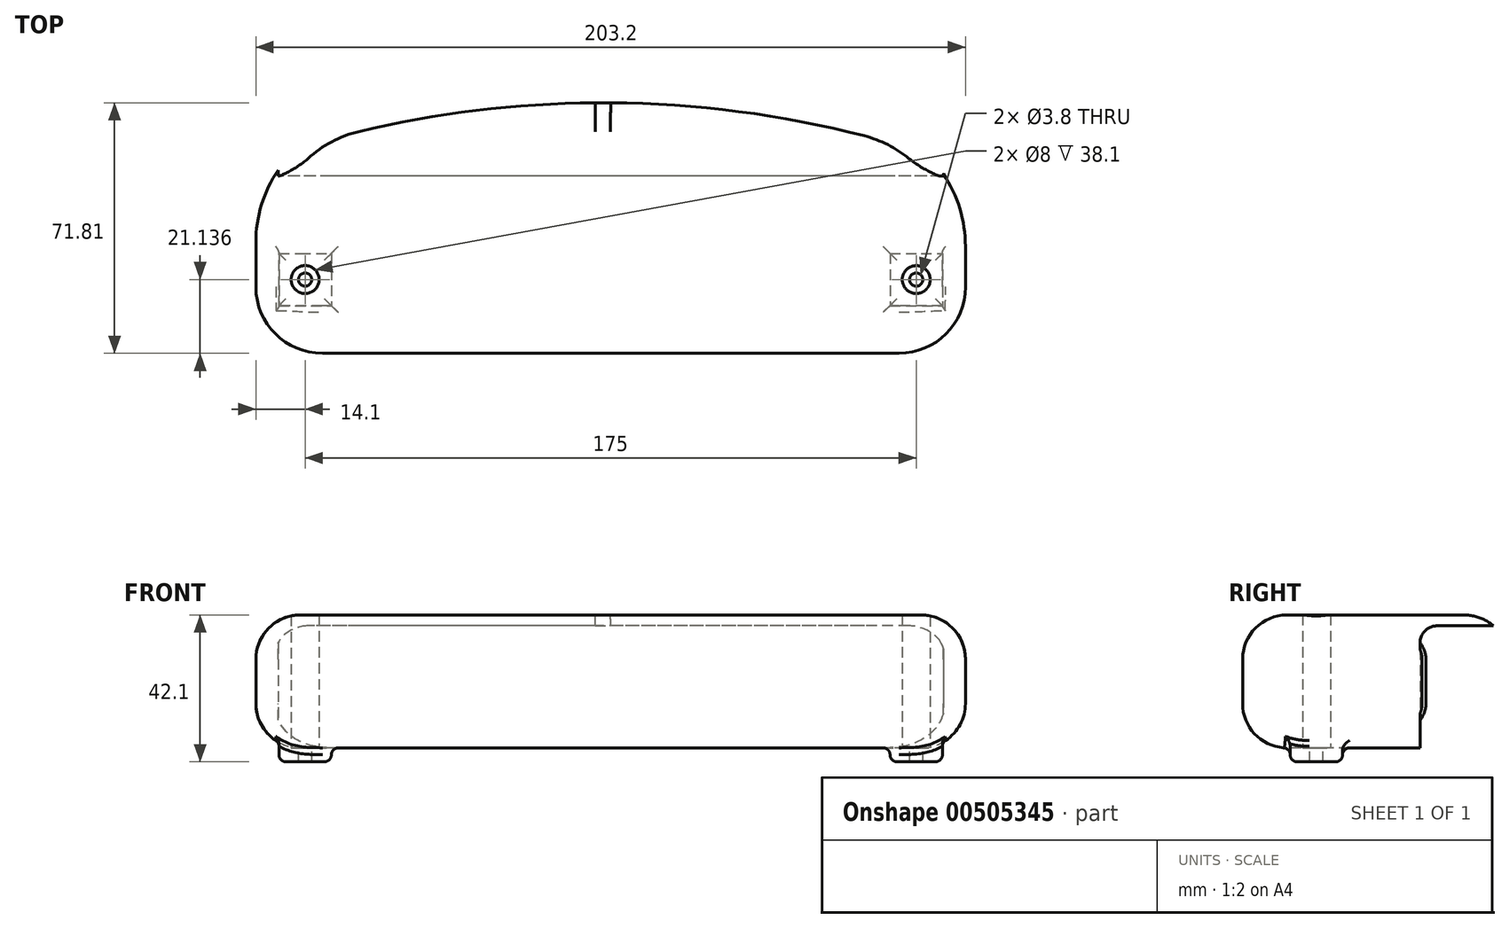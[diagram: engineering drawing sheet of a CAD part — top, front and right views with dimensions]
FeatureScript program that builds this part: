
annotation { "Feature Type Name" : "Feature", "Feature Type Description" : "" }
export const myFeature = defineFeature(function(context is Context, id is Id, definition is map)
    precondition{}
    {
        {
            var Q0;
            Q0=qCreatedBy(makeId("Top.planeOp"),FACE);
            var sketch = newSketch(context, id + "F0", { "sketchPlane" : qUnion([Q0])});
            skLineSegment(sketch, "E0.bottom", {"start": v(82.55, -38.1) * mm, "end": v(-82.55, -38.1) * mm});
            skLineSegment(sketch, "E0.top", {"start": v(0, 38.1) * mm, "end": v(-4.47, 38.1) * mm});
            skLineSegment(sketch, "E0.left", {"start": v(101.6, -19.05) * mm, "end": v(101.6, -7.46) * mm});
            skLineSegment(sketch, "E0.right", {"start": v(-101.6, -19.05) * mm, "end": v(-101.6, -6.35) * mm});
            skPoint(sketch, "E0.middle", {"position": v(0, 0) * mm});
            skPoint(sketch, "E1.visualSharp", {"position": v(-101.6, -38.1) * mm});
            skArc(sketch, "E1.filletArc", {"start": v(-101.6, -19.05) * mm, "mid": v(-96.02, -32.52) * mm, "end": v(-82.55, -38.1) * mm});
            skPoint(sketch, "E2.visualSharp", {"position": v(101.6, -38.1) * mm});
            skArc(sketch, "E2.filletArc", {"start": v(82.55, -38.1) * mm, "mid": v(96.02, -32.52) * mm, "end": v(101.6, -19.05) * mm});
            skArc(sketch, "E3", {"start": v(73.73, 28.49) * mm, "mid": v(0.39, 38.1) * mm, "end": v(-73.11, 29.75) * mm});
            skPoint(sketch, "E4", {"position": v(0, 38.1) * mm});
            skArc(sketch, "E5", {"start": v(-73.11, 29.75) * mm, "mid": v(-93.62, 16.65) * mm, "end": v(-101.6, -6.35) * mm});
            skArc(sketch, "E6", {"start": v(101.6, -7.46) * mm, "mid": v(93.82, 15.28) * mm, "end": v(73.73, 28.49) * mm});
            skPoint(sketch, "E7.orphan", {"position": v(101.6, 38.1) * mm});
            skPoint(sketch, "E8.trimOffspring.end.orphan", {"position": v(-101.6, 38.1) * mm});
            skPoint(sketch, "E9", {"position": v(-87.5, -16.96) * mm});
            skPoint(sketch, "E10", {"position": v(87.5, -16.96) * mm});
            skLineSegment(sketch, "E11", {"start": v(0, 0) * mm, "end": v(0, -38.1) * mm});
            skSolve(sketch);
        }
        {
            var Q0;
            Q0=makeQuery(id+"F0.imprint","IMPRINT",FACE,{"disambiguationData":[TD([[makeQuery(id+"F0.imprint","IMPRINT",EDGE,{"derivedFrom":sQuery(id+"F0.wireOp",EDGE,"E0.bottom")}),-1.0]])]});
            extrude(context, id + "F1", {"entities" : qUnion([Q0]), "depth" : 38.1 * mm});
        }
        {
            var Q0;
            Q0=makeQuery(id+"F1.opExtrude","CAP_EDGE",EDGE,{"disambiguationData":[OSD([sQuery(id+"F0.wireOp",EDGE,"E0.bottom")])],"isStart":false});
            var Q1;
            {var subQ0=sQuery(id+"F0.wireOp",EDGE,"E3");Q1=makeQuery(id+"F1.opExtrude","CAP_EDGE",EDGE,{"disambiguationData":[OSD([subQ0]),TDD([makeQuery(id+"F0.imprint","IMPRINT",EDGE,{"disambiguationData":[TD([[makeQuery(id+"F0.imprint","INTERSECT",VERTEX,{"disambiguationData":[OD(0.0)],"derivedFrom":[sQuery(id+"F0.wireOp",EDGE,"E0.top"),subQ0]}),1.0]])],"derivedFrom":subQ0})])],"isStart":true});}
            fillet(context, id + "F2", {"entities" : qUnion([Q0, Q1]), "radius" : 12.7 * mm, "tangentPropagation" : true, "allowEdgeOverflow" : false});
        }
        {
            var Q0;
            Q0=makeQuery(id+"F1.opExtrude","CAP_FACE",FACE,{"disambiguationData":[OSD([sQuery(id+"F0.wireOp",EDGE,"E0.bottom"),sQuery(id+"F0.wireOp",EDGE,"E0.top"),sQuery(id+"F0.wireOp",EDGE,"E0.left"),sQuery(id+"F0.wireOp",EDGE,"E0.right"),sQuery(id+"F0.wireOp",EDGE,"E1.filletArc"),sQuery(id+"F0.wireOp",EDGE,"E2.filletArc"),sQuery(id+"F0.wireOp",EDGE,"E3"),sQuery(id+"F0.wireOp",EDGE,"E5"),sQuery(id+"F0.wireOp",EDGE,"E6")])],"isStart":true});
            var sketch = newSketch(context, id + "F3", { "sketchPlane" : qUnion([Q0])});
            skLineSegment(sketch, "E12.bottom", {"start": v(80, 9.46) * mm, "end": v(95, 9.46) * mm});
            skLineSegment(sketch, "E12.top", {"start": v(80, 24.46) * mm, "end": v(95, 24.46) * mm});
            skLineSegment(sketch, "E12.left", {"start": v(80, 9.46) * mm, "end": v(80, 24.46) * mm});
            skLineSegment(sketch, "E12.right", {"start": v(95, 9.46) * mm, "end": v(95, 24.46) * mm});
            skPoint(sketch, "E12.middle", {"position": v(87.5, 16.96) * mm});
            skPoint(sketch, "E12.middle.positionSnap0", {"position": v(87.04, 23.54) * mm});
            skPoint(sketch, "E12.centerSnap0", {"position": v(87.04, 23.54) * mm});
            skLineSegment(sketch, "E13.bottom", {"start": v(-95, 9.46) * mm, "end": v(-80, 9.46) * mm});
            skLineSegment(sketch, "E13.top", {"start": v(-95, 24.46) * mm, "end": v(-80, 24.46) * mm});
            skLineSegment(sketch, "E13.left", {"start": v(-95, 9.46) * mm, "end": v(-95, 24.46) * mm});
            skLineSegment(sketch, "E13.right", {"start": v(-80, 9.46) * mm, "end": v(-80, 24.46) * mm});
            skPoint(sketch, "E13.middle", {"position": v(-87.5, 16.96) * mm});
            skSolve(sketch);
        }
        {
            var Q0;
            Q0 = qSketchRegion(id + "F3", true);
            extrude(context, id + "F4", {"entities" : qUnion([Q0]), "operationType" : NewBodyOperationType.ADD, "depth" : 4 * mm, "hasSecondDirection" : true, "secondDirectionOppositeDirection" : true, "secondDirectionDepth" : 8 * mm});
        }
        {
            var Q0;
            Q0=makeQuery(id+"F4.opExtrude","CAP_EDGE",EDGE,{"disambiguationData":[OSD([sQuery(id+"F3.wireOp",EDGE,"E12.right")])],"isStart":false});
            var Q1;
            {var subQ0=sQuery(id+"F0.wireOp",EDGE,"E0.left");Q1=makeQuery(id+"F4.boolean.opBoolean","INTERSECT",EDGE,{"derivedFrom":[makeQuery(id+"F2.opFillet","BLEND_FACE",FACE,{"disambiguationData":[OSD([subQ0]),TDD([makeQuery(id+"F1.opExtrude","CAP_EDGE",EDGE,{"disambiguationData":[OSD([subQ0])],"isStart":true})])]}),makeQuery(id+"F4.opExtrude","SWEPT_FACE",FACE,{"disambiguationData":[OSD([sQuery(id+"F3.wireOp",EDGE,"E12.right")])]})]});}
            var Q2;
            Q2=makeQuery(id+"F4.boolean.opBoolean","INTERSECT",EDGE,{"derivedFrom":[makeQuery(id+"F1.opExtrude","CAP_FACE",FACE,{"disambiguationData":[OSD([sQuery(id+"F0.wireOp",EDGE,"E0.bottom"),sQuery(id+"F0.wireOp",EDGE,"E0.top"),sQuery(id+"F0.wireOp",EDGE,"E0.left"),sQuery(id+"F0.wireOp",EDGE,"E0.right"),sQuery(id+"F0.wireOp",EDGE,"E1.filletArc"),sQuery(id+"F0.wireOp",EDGE,"E2.filletArc"),sQuery(id+"F0.wireOp",EDGE,"E3"),sQuery(id+"F0.wireOp",EDGE,"E5"),sQuery(id+"F0.wireOp",EDGE,"E6")])],"isStart":true}),makeQuery(id+"F4.opExtrude","SWEPT_FACE",FACE,{"disambiguationData":[OSD([sQuery(id+"F3.wireOp",EDGE,"E12.left")])]})]});
            var Q3;
            Q3=makeQuery(id+"F4.boolean.opBoolean","INTERSECT",EDGE,{"derivedFrom":[makeQuery(id+"F1.opExtrude","CAP_FACE",FACE,{"disambiguationData":[OSD([sQuery(id+"F0.wireOp",EDGE,"E0.bottom"),sQuery(id+"F0.wireOp",EDGE,"E0.top"),sQuery(id+"F0.wireOp",EDGE,"E0.left"),sQuery(id+"F0.wireOp",EDGE,"E0.right"),sQuery(id+"F0.wireOp",EDGE,"E1.filletArc"),sQuery(id+"F0.wireOp",EDGE,"E2.filletArc"),sQuery(id+"F0.wireOp",EDGE,"E3"),sQuery(id+"F0.wireOp",EDGE,"E5"),sQuery(id+"F0.wireOp",EDGE,"E6")])],"isStart":true}),makeQuery(id+"F4.opExtrude","SWEPT_FACE",FACE,{"disambiguationData":[OSD([sQuery(id+"F3.wireOp",EDGE,"E12.bottom")])]})]});
            var Q4;
            Q4=makeQuery(id+"F4.opExtrude","CAP_EDGE",EDGE,{"disambiguationData":[OSD([sQuery(id+"F3.wireOp",EDGE,"E12.bottom")])],"isStart":false});
            var Q5;
            Q5=makeQuery(id+"F4.opExtrude","CAP_EDGE",EDGE,{"disambiguationData":[OSD([sQuery(id+"F3.wireOp",EDGE,"E12.left")])],"isStart":false});
            var Q6;
            {var subQ0=sQuery(id+"F0.wireOp",EDGE,"E2.filletArc");Q6=makeQuery(id+"F4.boolean.opBoolean","INTERSECT",EDGE,{"derivedFrom":[makeQuery(id+"F2.opFillet","BLEND_FACE",FACE,{"disambiguationData":[OSD([subQ0]),TDD([makeQuery(id+"F1.opExtrude","CAP_EDGE",EDGE,{"disambiguationData":[OSD([subQ0])],"isStart":true})])]}),makeQuery(id+"F4.opExtrude","SWEPT_FACE",FACE,{"disambiguationData":[OSD([sQuery(id+"F3.wireOp",EDGE,"E12.top")])]})]});}
            var Q7;
            Q7=makeQuery(id+"F4.opExtrude","CAP_EDGE",EDGE,{"disambiguationData":[OSD([sQuery(id+"F3.wireOp",EDGE,"E12.top")])],"isStart":false});
            var Q8;
            Q8=makeQuery(id+"F4.opExtrude","CAP_EDGE",EDGE,{"disambiguationData":[OSD([sQuery(id+"F3.wireOp",EDGE,"E13.top")])],"isStart":false});
            var Q9;
            Q9=makeQuery(id+"F4.opExtrude","CAP_EDGE",EDGE,{"disambiguationData":[OSD([sQuery(id+"F3.wireOp",EDGE,"E13.right")])],"isStart":false});
            var Q10;
            Q10=makeQuery(id+"F4.opExtrude","CAP_EDGE",EDGE,{"disambiguationData":[OSD([sQuery(id+"F3.wireOp",EDGE,"E13.bottom")])],"isStart":false});
            var Q11;
            Q11=makeQuery(id+"F4.opExtrude","CAP_EDGE",EDGE,{"disambiguationData":[OSD([sQuery(id+"F3.wireOp",EDGE,"E13.left")])],"isStart":false});
            var Q12;
            Q12=makeQuery(id+"F4.boolean.opBoolean","INTERSECT",EDGE,{"derivedFrom":[makeQuery(id+"F1.opExtrude","CAP_FACE",FACE,{"disambiguationData":[OSD([sQuery(id+"F0.wireOp",EDGE,"E0.bottom"),sQuery(id+"F0.wireOp",EDGE,"E0.top"),sQuery(id+"F0.wireOp",EDGE,"E0.left"),sQuery(id+"F0.wireOp",EDGE,"E0.right"),sQuery(id+"F0.wireOp",EDGE,"E1.filletArc"),sQuery(id+"F0.wireOp",EDGE,"E2.filletArc"),sQuery(id+"F0.wireOp",EDGE,"E3"),sQuery(id+"F0.wireOp",EDGE,"E5"),sQuery(id+"F0.wireOp",EDGE,"E6")])],"isStart":true}),makeQuery(id+"F4.opExtrude","SWEPT_FACE",FACE,{"disambiguationData":[OSD([sQuery(id+"F3.wireOp",EDGE,"E13.top")])]})]});
            var Q13;
            Q13=makeQuery(id+"F4.boolean.opBoolean","INTERSECT",EDGE,{"derivedFrom":[makeQuery(id+"F1.opExtrude","CAP_FACE",FACE,{"disambiguationData":[OSD([sQuery(id+"F0.wireOp",EDGE,"E0.bottom"),sQuery(id+"F0.wireOp",EDGE,"E0.top"),sQuery(id+"F0.wireOp",EDGE,"E0.left"),sQuery(id+"F0.wireOp",EDGE,"E0.right"),sQuery(id+"F0.wireOp",EDGE,"E1.filletArc"),sQuery(id+"F0.wireOp",EDGE,"E2.filletArc"),sQuery(id+"F0.wireOp",EDGE,"E3"),sQuery(id+"F0.wireOp",EDGE,"E5"),sQuery(id+"F0.wireOp",EDGE,"E6")])],"isStart":true}),makeQuery(id+"F4.opExtrude","SWEPT_FACE",FACE,{"disambiguationData":[OSD([sQuery(id+"F3.wireOp",EDGE,"E13.right")])]})]});
            var Q14;
            {var subQ0=sQuery(id+"F0.wireOp",EDGE,"E0.right");Q14=makeQuery(id+"F4.boolean.opBoolean","INTERSECT",EDGE,{"derivedFrom":[makeQuery(id+"F2.opFillet","BLEND_FACE",FACE,{"disambiguationData":[OSD([subQ0]),TDD([makeQuery(id+"F1.opExtrude","CAP_EDGE",EDGE,{"disambiguationData":[OSD([subQ0])],"isStart":true})])]}),makeQuery(id+"F4.opExtrude","SWEPT_FACE",FACE,{"disambiguationData":[OSD([sQuery(id+"F3.wireOp",EDGE,"E13.left")])]})]});}
            var Q15;
            Q15=makeQuery(id+"F4.boolean.opBoolean","INTERSECT",EDGE,{"derivedFrom":[makeQuery(id+"F1.opExtrude","CAP_FACE",FACE,{"disambiguationData":[OSD([sQuery(id+"F0.wireOp",EDGE,"E0.bottom"),sQuery(id+"F0.wireOp",EDGE,"E0.top"),sQuery(id+"F0.wireOp",EDGE,"E0.left"),sQuery(id+"F0.wireOp",EDGE,"E0.right"),sQuery(id+"F0.wireOp",EDGE,"E1.filletArc"),sQuery(id+"F0.wireOp",EDGE,"E2.filletArc"),sQuery(id+"F0.wireOp",EDGE,"E3"),sQuery(id+"F0.wireOp",EDGE,"E5"),sQuery(id+"F0.wireOp",EDGE,"E6")])],"isStart":true}),makeQuery(id+"F4.opExtrude","SWEPT_FACE",FACE,{"disambiguationData":[OSD([sQuery(id+"F3.wireOp",EDGE,"E13.bottom")])]})]});
            fillet(context, id + "F5", {"entities" : qUnion([Q0, Q1, Q2, Q3, Q4, Q5, Q6, Q7, Q8, Q9, Q10, Q11, Q12, Q13, Q14, Q15]), "radius" : 2 * mm, "tangentPropagation" : true, "allowEdgeOverflow" : false});
        }
        {
            var Q0;
            Q0=qCreatedBy(makeId("Top.planeOp"),FACE);
            var sketch = newSketch(context, id + "F6", { "sketchPlane" : qUnion([Q0])});
            skLineSegment(sketch, "E14.bottom", {"start": v(95.25, 12.7) * mm, "end": v(-95.25, 12.7) * mm});
            skLineSegment(sketch, "E14.top", {"start": v(95.25, 63.5) * mm, "end": v(-95.25, 63.5) * mm});
            skLineSegment(sketch, "E14.left", {"start": v(95.25, 12.7) * mm, "end": v(95.25, 63.5) * mm});
            skLineSegment(sketch, "E14.right", {"start": v(-95.25, 12.7) * mm, "end": v(-95.25, 63.5) * mm});
            skPoint(sketch, "E14.middle", {"position": v(0, 38.1) * mm});
            skSolve(sketch);
        }
        {
            var Q0;
            Q0=makeQuery(id+"F6.imprint","IMPRINT",FACE,{"disambiguationData":[TD([[makeQuery(id+"F6.imprint","IMPRINT",EDGE,{"derivedFrom":sQuery(id+"F6.wireOp",EDGE,"E14.bottom")}),-1.0]])]});
            extrude(context, id + "F7", {"entities" : qUnion([Q0]), "operationType" : NewBodyOperationType.REMOVE, "depth" : 35 * mm});
        }
        {
            var Q0;
            {var subQ0=sQuery(id+"F0.wireOp",EDGE,"E6");var subQ1=makeQuery(id+"F2.opFillet","BLEND_FACE",FACE,{"disambiguationData":[OSD([subQ0]),TDD([makeQuery(id+"F1.opExtrude","CAP_EDGE",EDGE,{"disambiguationData":[OSD([subQ0])],"isStart":false})])]});var subQ2=sQuery(id+"F6.wireOp",EDGE,"E14.bottom");Q0=makeQuery(id+"F7.boolean.opBoolean","COPY",EDGE,{"disambiguationData":[TD([subQ1])],"derivedFrom":makeQuery(id+"F7.opExtrude","CAP_EDGE",EDGE,{"disambiguationData":[OSD([subQ2])],"isStart":false})});}
            var Q1;
            {var subQ0=sQuery(id+"F0.wireOp",EDGE,"E5");var subQ1=makeQuery(id+"F2.opFillet","BLEND_FACE",FACE,{"disambiguationData":[OSD([subQ0]),TDD([makeQuery(id+"F1.opExtrude","CAP_EDGE",EDGE,{"disambiguationData":[OSD([subQ0])],"isStart":false})])]});var subQ2=sQuery(id+"F6.wireOp",EDGE,"E14.bottom");Q1=makeQuery(id+"F7.boolean.opBoolean","COPY",EDGE,{"disambiguationData":[TD([subQ1])],"derivedFrom":makeQuery(id+"F7.opExtrude","CAP_EDGE",EDGE,{"disambiguationData":[OSD([subQ2])],"isStart":false})});}
            fillet(context, id + "F8", {"entities" : qUnion([Q0, Q1]), "radius" : 5 * mm, "tangentPropagation" : true, "allowEdgeOverflow" : false});
        }
        {
            var Q0;
            Q0=sQuery(id+"F0.wireOp",VERTEX,"E10");
            var Q1;
            Q1=sQuery(id+"F0.wireOp",VERTEX,"E9");
            var Q2;
            Q2=makeQuery(id+"F1.opExtrude","SWEPT_BODY",BODY,{"disambiguationData":[OSD([sQuery(id+"F0.wireOp",EDGE,"E0.bottom"),sQuery(id+"F0.wireOp",EDGE,"E0.top"),sQuery(id+"F0.wireOp",EDGE,"E0.left"),sQuery(id+"F0.wireOp",EDGE,"E0.right"),sQuery(id+"F0.wireOp",EDGE,"E1.filletArc"),sQuery(id+"F0.wireOp",EDGE,"E2.filletArc"),sQuery(id+"F0.wireOp",EDGE,"E3"),sQuery(id+"F0.wireOp",EDGE,"E5"),sQuery(id+"F0.wireOp",EDGE,"E6")])]});
            hole(context, id + "F9", {"style" : HoleStyle.SIMPLE, "endStyle" : HoleEndStyle.THROUGH, "standardTappedOrClearance" : lookupTablePath({ "standard" : "ANSI", "fit" : "Normal (ASME)", "size" : "#6", "type" : "Clearance" }), "standardBlindInLast" : lookupTablePath({ "fit" : "Free", "standard" : "ANSI", "size" : "#6", "type" : "Clearance" }), "holeDiameter" : 3.8 * mm, "isTappedThrough" : true, "tappedDepth" : 12.7 * mm, "tapClearance" : 3, "locations" : qUnion([Q0, Q1]), "scope" : qUnion([Q2])});
        }
        {
            var Q0;
            Q0=sQuery(id+"F0.wireOp",VERTEX,"E9");
            var Q1;
            Q1=sQuery(id+"F0.wireOp",VERTEX,"E10");
            var Q2;
            Q2=makeQuery(id+"F1.opExtrude","SWEPT_BODY",BODY,{"disambiguationData":[OSD([sQuery(id+"F0.wireOp",EDGE,"E0.bottom"),sQuery(id+"F0.wireOp",EDGE,"E0.top"),sQuery(id+"F0.wireOp",EDGE,"E0.left"),sQuery(id+"F0.wireOp",EDGE,"E0.right"),sQuery(id+"F0.wireOp",EDGE,"E1.filletArc"),sQuery(id+"F0.wireOp",EDGE,"E2.filletArc"),sQuery(id+"F0.wireOp",EDGE,"E3"),sQuery(id+"F0.wireOp",EDGE,"E5"),sQuery(id+"F0.wireOp",EDGE,"E6")])]});
            hole(context, id + "F10", {"style" : HoleStyle.SIMPLE, "endStyle" : HoleEndStyle.THROUGH, "oppositeDirection" : true, "holeDiameter" : 8 * mm, "isTappedThrough" : true, "tappedDepth" : 12.7 * mm, "tapClearance" : 3, "startFromSketch" : true, "locations" : qUnion([Q0, Q1]), "scope" : qUnion([Q2])});
        }
    });
